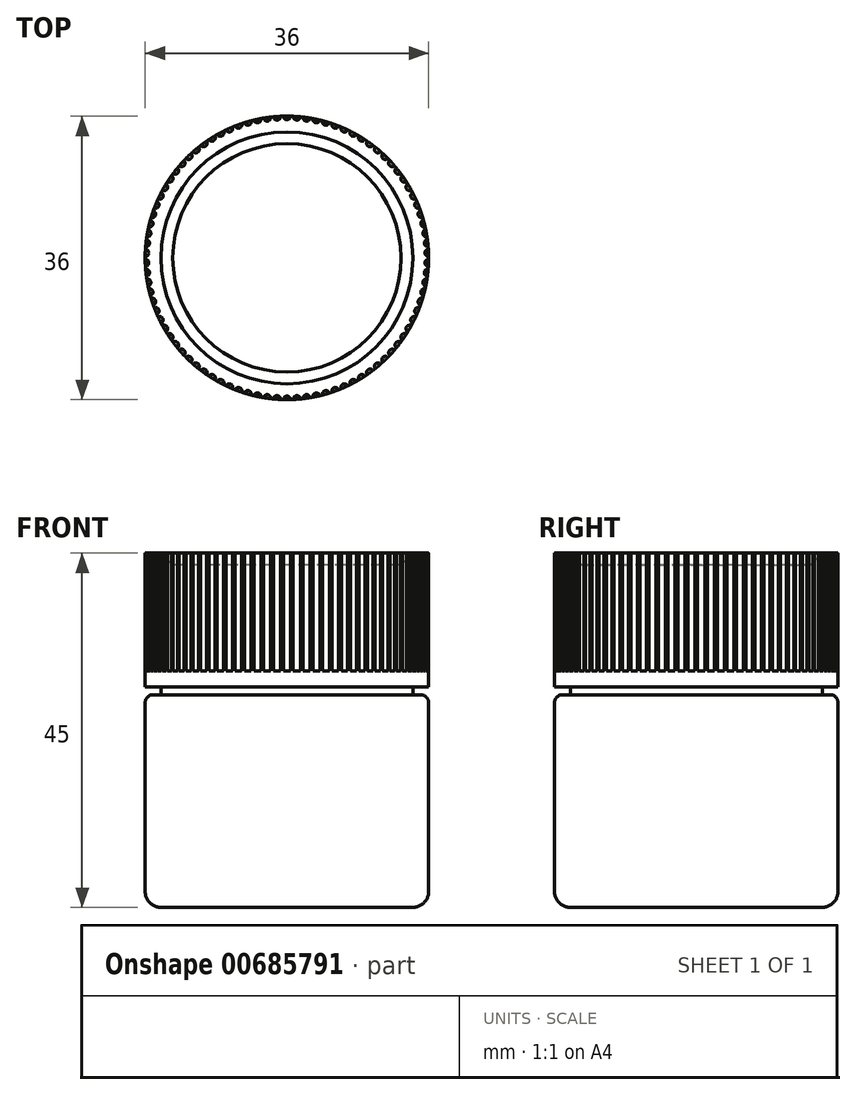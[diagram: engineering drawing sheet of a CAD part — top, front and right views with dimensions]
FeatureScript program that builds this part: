
annotation { "Feature Type Name" : "Feature", "Feature Type Description" : "" }
export const myFeature = defineFeature(function(context is Context, id is Id, definition is map)
    precondition{}
    {
        {
            var Q0;
            Q0=qCreatedBy(makeId("Top.planeOp"),FACE);
            var sketch = newSketch(context, id + "F0", { "sketchPlane" : qUnion([Q0])});
            skCircle(sketch, "E0", {"center": v(0, 0) * mm, "radius": 18 * mm});
            skSolve(sketch);
        }
        {
            var Q0;
            Q0 = qSketchRegion(id + "F0", true);
            extrude(context, id + "F1", {"entities" : qUnion([Q0]), "depth" : 27 * mm, "offsetDistance" : 25 * mm});
        }
        {
            var Q0;
            Q0=makeQuery(id+"F1.opExtrude","CAP_FACE",FACE,{"disambiguationData":[OSD([sQuery(id+"F0.wireOp",EDGE,"E0")])],"isStart":false});
            var sketch = newSketch(context, id + "F2", { "sketchPlane" : qUnion([Q0])});
            skCircle(sketch, "E1", {"center": v(0, 0) * mm, "radius": 16 * mm});
            skSolve(sketch);
        }
        {
            var Q0;
            Q0 = qSketchRegion(id + "F2", true);
            extrude(context, id + "F3", {"entities" : qUnion([Q0]), "operationType" : NewBodyOperationType.ADD, "depth" : 1 * mm, "offsetDistance" : 25 * mm});
        }
        {
            var Q0;
            Q0=makeQuery(id+"F3.opExtrude","CAP_FACE",FACE,{"disambiguationData":[OSD([sQuery(id+"F2.wireOp",EDGE,"E1")])],"isStart":false});
            var sketch = newSketch(context, id + "F4", { "sketchPlane" : qUnion([Q0])});
            skCircle(sketch, "E2", {"center": v(0, 0) * mm, "radius": 18 * mm});
            skSolve(sketch);
        }
        {
            var Q0;
            Q0 = qSketchRegion(id + "F4", true);
            extrude(context, id + "F5", {"entities" : qUnion([Q0]), "operationType" : NewBodyOperationType.ADD, "depth" : 17 * mm, "offsetDistance" : 25 * mm});
        }
        {
            var Q0;
            Q0=makeQuery(id+"F1.opExtrude","CAP_FACE",FACE,{"disambiguationData":[OSD([sQuery(id+"F0.wireOp",EDGE,"E0")])],"isStart":true});
            fillet(context, id + "F6", {"entities" : qUnion([Q0]), "radius" : 2 * mm, "tangentPropagation" : true, "allowEdgeOverflow" : false});
        }
        {
            var Q0;
            Q0=makeQuery(id+"F1.opExtrude","CAP_EDGE",EDGE,{"disambiguationData":[OSD([sQuery(id+"F0.wireOp",EDGE,"E0")])],"isStart":false});
            var Q1;
            Q1=makeQuery(id+"F3.opExtrude","CAP_EDGE",EDGE,{"disambiguationData":[OSD([sQuery(id+"F2.wireOp",EDGE,"E1")])],"isStart":true});
            fillet(context, id + "F7", {"entities" : qUnion([Q0, Q1]), "radius" : 1 * mm, "tangentPropagation" : true, "allowEdgeOverflow" : false});
        }
        {
            var Q0;
            Q0=makeQuery(id+"F5.opExtrude","CAP_FACE",FACE,{"disambiguationData":[OSD([sQuery(id+"F4.wireOp",EDGE,"E2")])],"isStart":false});
            var sketch = newSketch(context, id + "F8", { "sketchPlane" : qUnion([Q0])});
            skCircle(sketch, "E3", {"center": v(0, 0) * mm, "radius": 16 * mm});
            skSolve(sketch);
        }
        {
            var Q0;
            Q0 = qSketchRegion(id + "F8", true);
            extrude(context, id + "F9", {"entities" : qUnion([Q0]), "operationType" : NewBodyOperationType.REMOVE, "oppositeDirection" : true, "depth" : 1.5 * mm, "offsetDistance" : 25 * mm, "hasDraft" : true, "draftAngle" : 45 * degree, "draftPullDirection" : true});
        }
        {
            var Q0;
            Q0=makeQuery(id+"F5.opExtrude","CAP_FACE",FACE,{"disambiguationData":[OSD([sQuery(id+"F4.wireOp",EDGE,"E2")])],"isStart":false});
            var sketch = newSketch(context, id + "F10", { "sketchPlane" : qUnion([Q0])});
            skCircle(sketch, "E4", {"center": v(0, 18) * mm, "radius": 0.45 * mm});
            skCircle(sketch, "E5.1.0", {"center": v(-1.26, 17.96) * mm, "radius": 0.45 * mm});
            skCircle(sketch, "E5.2.0", {"center": v(-2.5, 17.82) * mm, "radius": 0.45 * mm});
            skCircle(sketch, "E5.3.0", {"center": v(-3.74, 17.6) * mm, "radius": 0.45 * mm});
            skCircle(sketch, "E5.4.0", {"center": v(-4.96, 17.3) * mm, "radius": 0.45 * mm});
            skCircle(sketch, "E5.5.0", {"center": v(-6.16, 16.91) * mm, "radius": 0.45 * mm});
            skCircle(sketch, "E5.6.0", {"center": v(-7.32, 16.44) * mm, "radius": 0.45 * mm});
            skCircle(sketch, "E5.7.0", {"center": v(-8.45, 15.9) * mm, "radius": 0.45 * mm});
            skCircle(sketch, "E5.8.0", {"center": v(-9.54, 15.26) * mm, "radius": 0.45 * mm});
            skCircle(sketch, "E5.9.0", {"center": v(-10.58, 14.56) * mm, "radius": 0.45 * mm});
            skCircle(sketch, "E5.10.0", {"center": v(-11.57, 13.79) * mm, "radius": 0.45 * mm});
            skCircle(sketch, "E5.11.0", {"center": v(-12.5, 12.95) * mm, "radius": 0.45 * mm});
            skCircle(sketch, "E5.12.0", {"center": v(-13.38, 12.04) * mm, "radius": 0.45 * mm});
            skCircle(sketch, "E5.13.0", {"center": v(-14.18, 11.08) * mm, "radius": 0.45 * mm});
            skCircle(sketch, "E5.14.0", {"center": v(-14.92, 10.07) * mm, "radius": 0.45 * mm});
            skCircle(sketch, "E5.15.0", {"center": v(-15.59, 9) * mm, "radius": 0.45 * mm});
            skCircle(sketch, "E5.16.0", {"center": v(-16.18, 7.9) * mm, "radius": 0.45 * mm});
            skCircle(sketch, "E5.17.0", {"center": v(-16.69, 6.74) * mm, "radius": 0.45 * mm});
            skCircle(sketch, "E5.18.0", {"center": v(-17.12, 5.56) * mm, "radius": 0.45 * mm});
            skCircle(sketch, "E5.19.0", {"center": v(-17.47, 4.35) * mm, "radius": 0.45 * mm});
            skCircle(sketch, "E5.20.0", {"center": v(-17.73, 3.13) * mm, "radius": 0.45 * mm});
            skCircle(sketch, "E5.21.0", {"center": v(-17.9, 1.88) * mm, "radius": 0.45 * mm});
            skCircle(sketch, "E5.22.0", {"center": v(-17.99, 0.63) * mm, "radius": 0.45 * mm});
            skCircle(sketch, "E5.23.0", {"center": v(-17.99, -0.63) * mm, "radius": 0.45 * mm});
            skCircle(sketch, "E5.24.0", {"center": v(-17.9, -1.88) * mm, "radius": 0.45 * mm});
            skCircle(sketch, "E5.25.0", {"center": v(-17.73, -3.13) * mm, "radius": 0.45 * mm});
            skCircle(sketch, "E5.26.0", {"center": v(-17.47, -4.35) * mm, "radius": 0.45 * mm});
            skCircle(sketch, "E5.27.0", {"center": v(-17.12, -5.56) * mm, "radius": 0.45 * mm});
            skCircle(sketch, "E5.28.0", {"center": v(-16.69, -6.74) * mm, "radius": 0.45 * mm});
            skCircle(sketch, "E5.29.0", {"center": v(-16.18, -7.9) * mm, "radius": 0.45 * mm});
            skCircle(sketch, "E5.30.0", {"center": v(-15.59, -9) * mm, "radius": 0.45 * mm});
            skCircle(sketch, "E5.31.0", {"center": v(-14.92, -10.07) * mm, "radius": 0.45 * mm});
            skCircle(sketch, "E5.32.0", {"center": v(-14.18, -11.08) * mm, "radius": 0.45 * mm});
            skCircle(sketch, "E5.33.0", {"center": v(-13.38, -12.04) * mm, "radius": 0.45 * mm});
            skCircle(sketch, "E5.34.0", {"center": v(-12.5, -12.95) * mm, "radius": 0.45 * mm});
            skCircle(sketch, "E5.35.0", {"center": v(-11.57, -13.79) * mm, "radius": 0.45 * mm});
            skCircle(sketch, "E5.36.0", {"center": v(-10.58, -14.56) * mm, "radius": 0.45 * mm});
            skCircle(sketch, "E5.37.0", {"center": v(-9.54, -15.26) * mm, "radius": 0.45 * mm});
            skCircle(sketch, "E5.38.0", {"center": v(-8.45, -15.9) * mm, "radius": 0.45 * mm});
            skCircle(sketch, "E5.39.0", {"center": v(-7.32, -16.44) * mm, "radius": 0.45 * mm});
            skCircle(sketch, "E5.40.0", {"center": v(-6.16, -16.91) * mm, "radius": 0.45 * mm});
            skCircle(sketch, "E5.41.0", {"center": v(-4.96, -17.3) * mm, "radius": 0.45 * mm});
            skCircle(sketch, "E5.42.0", {"center": v(-3.74, -17.6) * mm, "radius": 0.45 * mm});
            skCircle(sketch, "E5.43.0", {"center": v(-2.5, -17.82) * mm, "radius": 0.45 * mm});
            skCircle(sketch, "E5.44.0", {"center": v(-1.26, -17.96) * mm, "radius": 0.45 * mm});
            skCircle(sketch, "E5.45.0", {"center": v(0, -18) * mm, "radius": 0.45 * mm});
            skCircle(sketch, "E5.46.0", {"center": v(1.26, -17.96) * mm, "radius": 0.45 * mm});
            skCircle(sketch, "E5.47.0", {"center": v(2.5, -17.82) * mm, "radius": 0.45 * mm});
            skCircle(sketch, "E5.48.0", {"center": v(3.74, -17.6) * mm, "radius": 0.45 * mm});
            skCircle(sketch, "E5.49.0", {"center": v(4.96, -17.3) * mm, "radius": 0.45 * mm});
            skCircle(sketch, "E5.50.0", {"center": v(6.16, -16.91) * mm, "radius": 0.45 * mm});
            skCircle(sketch, "E5.51.0", {"center": v(7.32, -16.44) * mm, "radius": 0.45 * mm});
            skCircle(sketch, "E5.52.0", {"center": v(8.45, -15.9) * mm, "radius": 0.45 * mm});
            skCircle(sketch, "E5.53.0", {"center": v(9.54, -15.26) * mm, "radius": 0.45 * mm});
            skCircle(sketch, "E5.54.0", {"center": v(10.58, -14.56) * mm, "radius": 0.45 * mm});
            skCircle(sketch, "E5.55.0", {"center": v(11.57, -13.79) * mm, "radius": 0.45 * mm});
            skCircle(sketch, "E5.56.0", {"center": v(12.5, -12.95) * mm, "radius": 0.45 * mm});
            skCircle(sketch, "E5.57.0", {"center": v(13.38, -12.04) * mm, "radius": 0.45 * mm});
            skCircle(sketch, "E5.58.0", {"center": v(14.18, -11.08) * mm, "radius": 0.45 * mm});
            skCircle(sketch, "E5.59.0", {"center": v(14.92, -10.07) * mm, "radius": 0.45 * mm});
            skCircle(sketch, "E5.60.0", {"center": v(15.59, -9) * mm, "radius": 0.45 * mm});
            skCircle(sketch, "E5.61.0", {"center": v(16.18, -7.9) * mm, "radius": 0.45 * mm});
            skCircle(sketch, "E5.62.0", {"center": v(16.69, -6.74) * mm, "radius": 0.45 * mm});
            skCircle(sketch, "E5.63.0", {"center": v(17.12, -5.56) * mm, "radius": 0.45 * mm});
            skCircle(sketch, "E5.64.0", {"center": v(17.47, -4.35) * mm, "radius": 0.45 * mm});
            skCircle(sketch, "E5.65.0", {"center": v(17.73, -3.13) * mm, "radius": 0.45 * mm});
            skCircle(sketch, "E5.66.0", {"center": v(17.9, -1.88) * mm, "radius": 0.45 * mm});
            skCircle(sketch, "E5.67.0", {"center": v(17.99, -0.63) * mm, "radius": 0.45 * mm});
            skCircle(sketch, "E5.68.0", {"center": v(17.99, 0.63) * mm, "radius": 0.45 * mm});
            skCircle(sketch, "E5.69.0", {"center": v(17.9, 1.88) * mm, "radius": 0.45 * mm});
            skCircle(sketch, "E5.70.0", {"center": v(17.73, 3.13) * mm, "radius": 0.45 * mm});
            skCircle(sketch, "E5.71.0", {"center": v(17.47, 4.35) * mm, "radius": 0.45 * mm});
            skCircle(sketch, "E5.72.0", {"center": v(17.12, 5.56) * mm, "radius": 0.45 * mm});
            skCircle(sketch, "E5.73.0", {"center": v(16.69, 6.74) * mm, "radius": 0.45 * mm});
            skCircle(sketch, "E5.74.0", {"center": v(16.18, 7.9) * mm, "radius": 0.45 * mm});
            skCircle(sketch, "E5.75.0", {"center": v(15.59, 9) * mm, "radius": 0.45 * mm});
            skCircle(sketch, "E5.76.0", {"center": v(14.92, 10.07) * mm, "radius": 0.45 * mm});
            skCircle(sketch, "E5.77.0", {"center": v(14.18, 11.08) * mm, "radius": 0.45 * mm});
            skCircle(sketch, "E5.78.0", {"center": v(13.38, 12.04) * mm, "radius": 0.45 * mm});
            skCircle(sketch, "E5.79.0", {"center": v(12.5, 12.95) * mm, "radius": 0.45 * mm});
            skCircle(sketch, "E5.80.0", {"center": v(11.57, 13.79) * mm, "radius": 0.45 * mm});
            skCircle(sketch, "E5.81.0", {"center": v(10.58, 14.56) * mm, "radius": 0.45 * mm});
            skCircle(sketch, "E5.82.0", {"center": v(9.54, 15.26) * mm, "radius": 0.45 * mm});
            skCircle(sketch, "E5.83.0", {"center": v(8.45, 15.9) * mm, "radius": 0.45 * mm});
            skCircle(sketch, "E5.84.0", {"center": v(7.32, 16.44) * mm, "radius": 0.45 * mm});
            skCircle(sketch, "E5.85.0", {"center": v(6.16, 16.91) * mm, "radius": 0.45 * mm});
            skCircle(sketch, "E5.86.0", {"center": v(4.96, 17.3) * mm, "radius": 0.45 * mm});
            skCircle(sketch, "E5.87.0", {"center": v(3.74, 17.6) * mm, "radius": 0.45 * mm});
            skCircle(sketch, "E5.88.0", {"center": v(2.5, 17.82) * mm, "radius": 0.45 * mm});
            skCircle(sketch, "E5.89.0", {"center": v(1.26, 17.96) * mm, "radius": 0.45 * mm});
            skPoint(sketch, "E5.center", {"position": v(0, 0) * mm});
            skSolve(sketch);
        }
        {
            var Q0;
            Q0 = qSketchRegion(id + "F10", true);
            extrude(context, id + "F11", {"entities" : qUnion([Q0]), "operationType" : NewBodyOperationType.REMOVE, "oppositeDirection" : true, "depth" : 15 * mm, "offsetDistance" : 25 * mm});
        }
    });
